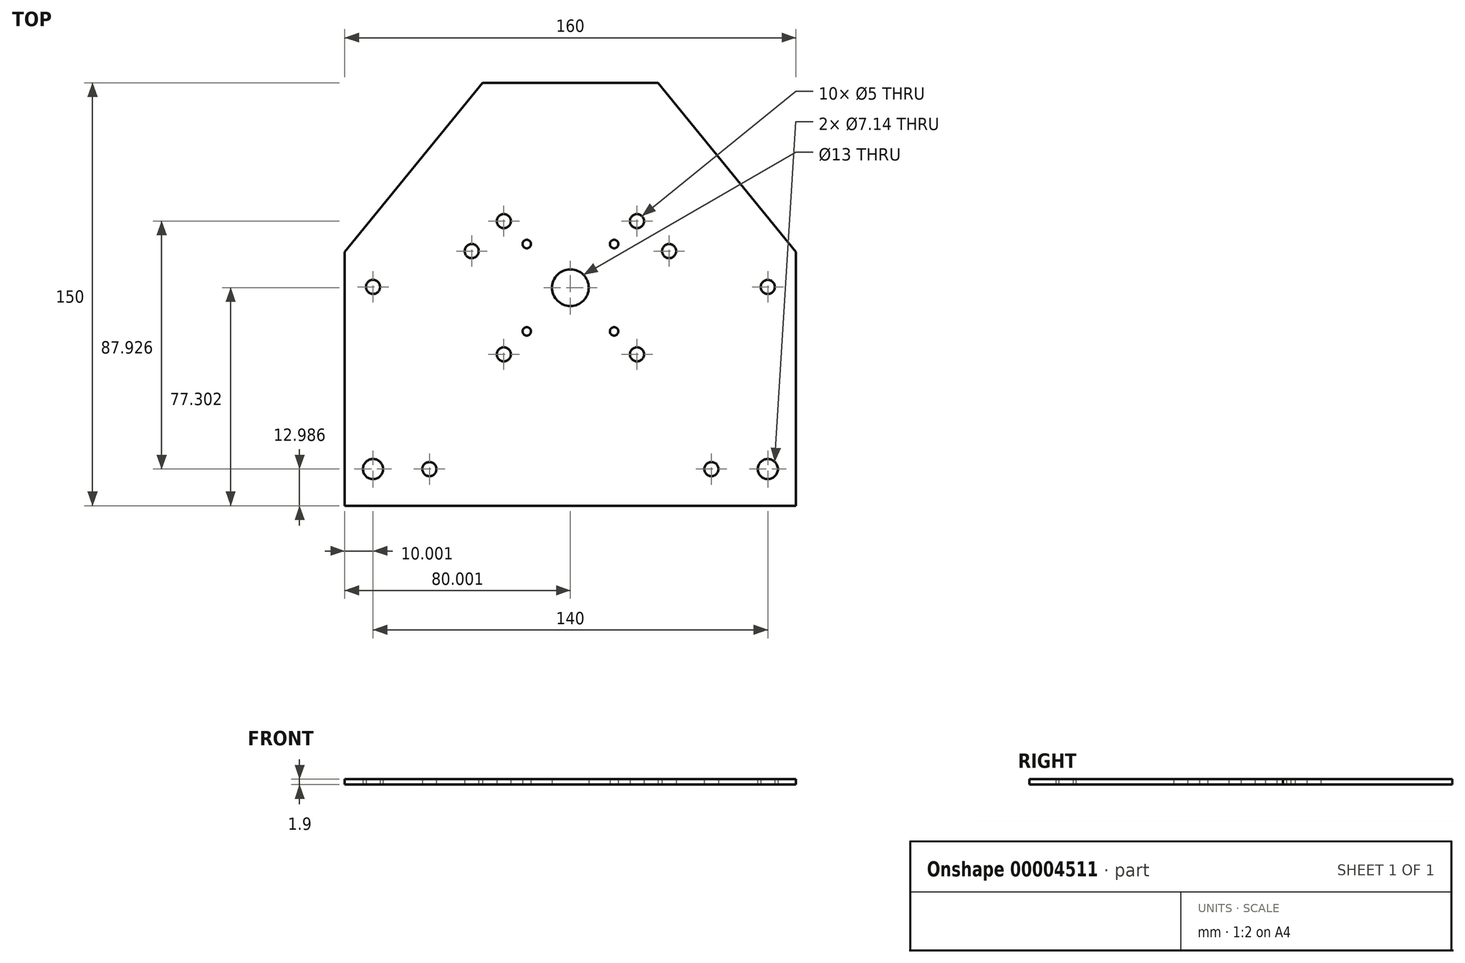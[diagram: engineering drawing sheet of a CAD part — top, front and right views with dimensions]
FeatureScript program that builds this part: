
annotation { "Feature Type Name" : "Feature", "Feature Type Description" : "" }
export const myFeature = defineFeature(function(context is Context, id is Id, definition is map)
    precondition{}
    {
        {
            var Q0;
            Q0=qCreatedBy(makeId("Top.planeOp"),FACE);
            var sketch = newSketch(context, id + "F0", { "sketchPlane" : qUnion([Q0])});
            skLineSegment(sketch, "E0.rect.left", {"start": v(-80.02, 15.3) * mm, "end": v(-80.02, -74.7) * mm});
            skLineSegment(sketch, "E0.rect.right", {"start": v(79.98, 15.3) * mm, "end": v(79.98, -74.7) * mm});
            skPoint(sketch, "E0.rect.middle", {"position": v(0, 0) * mm});
            skLineSegment(sketch, "E1", {"start": v(-80.02, 15.3) * mm, "end": v(-31.13, 75.3) * mm});
            skLineSegment(sketch, "E2", {"start": v(31.09, 75.3) * mm, "end": v(79.98, 15.3) * mm});
            skLineSegment(sketch, "E3", {"start": v(-0.02, 75.3) * mm, "end": v(-0.02, -74.7) * mm, "construction": true});
            skCircle(sketch, "E4", {"center": v(-70.02, -61.71) * mm, "radius": 3.57 * mm});
            skCircle(sketch, "E5", {"center": v(-50.02, -61.71) * mm, "radius": 2.5 * mm});
            skLineSegment(sketch, "E6", {"start": v(-70.02, -61.71) * mm, "end": v(-80.02, -61.71) * mm, "construction": true});
            skLineSegment(sketch, "E7", {"start": v(-70.02, -61.71) * mm, "end": v(-70.02, -74.41) * mm, "construction": true});
            skLineSegment(sketch, "E8", {"start": v(-50.02, -61.71) * mm, "end": v(-80.02, -61.71) * mm, "construction": true});
            skLineSegment(sketch, "E9", {"start": v(-50.02, -61.71) * mm, "end": v(-50.02, -74.41) * mm, "construction": true});
            skCircle(sketch, "E10", {"center": v(-70.02, 2.89) * mm, "radius": 2.5 * mm});
            skLineSegment(sketch, "E11", {"start": v(-70.02, 2.89) * mm, "end": v(-80.02, 2.89) * mm, "construction": true});
            skLineSegment(sketch, "E12", {"start": v(-70.02, 2.89) * mm, "end": v(-70.02, -74.41) * mm, "construction": true});
            skCircle(sketch, "E13", {"center": v(-35.02, 15.59) * mm, "radius": 2.5 * mm});
            skLineSegment(sketch, "E14", {"start": v(-35.02, 15.59) * mm, "end": v(-80.02, 15.59) * mm, "construction": true});
            skLineSegment(sketch, "E15", {"start": v(-35.02, 15.59) * mm, "end": v(-35.02, -74.41) * mm, "construction": true});
            skLineSegment(sketch, "E16", {"start": v(-31.13, 75.3) * mm, "end": v(-0.02, 75.3) * mm});
            skLineSegment(sketch, "E17", {"start": v(-0.02, 75.3) * mm, "end": v(31.09, 75.3) * mm});
            skCircle(sketch, "E18.0.MirrorC", {"center": v(69.98, -61.71) * mm, "radius": 3.57 * mm});
            skCircle(sketch, "E18.1.MirrorC", {"center": v(49.98, -61.71) * mm, "radius": 2.5 * mm});
            skCircle(sketch, "E18.2.MirrorC", {"center": v(34.98, 15.59) * mm, "radius": 2.5 * mm});
            skCircle(sketch, "E18.3.MirrorC", {"center": v(69.98, 2.89) * mm, "radius": 2.5 * mm});
            skLineSegment(sketch, "E19", {"start": v(-80.02, -74.7) * mm, "end": v(-0.02, -74.7) * mm});
            skLineSegment(sketch, "E20", {"start": v(-0.02, -74.7) * mm, "end": v(79.98, -74.7) * mm});
            skCircle(sketch, "E21", {"center": v(-23.63, -21.03) * mm, "radius": 2.5 * mm});
            skLineSegment(sketch, "E22", {"start": v(-23.63, -21.03) * mm, "end": v(-80.02, -21.03) * mm, "construction": true});
            skLineSegment(sketch, "E23", {"start": v(-23.63, -21.03) * mm, "end": v(-23.63, -74.7) * mm, "construction": true});
            skCircle(sketch, "E24.0.MirrorC", {"center": v(23.6, -21.03) * mm, "radius": 2.5 * mm});
            skCircle(sketch, "E25", {"center": v(-23.63, 26.21) * mm, "radius": 2.5 * mm});
            skLineSegment(sketch, "E26", {"start": v(-23.63, -74.7) * mm, "end": v(-23.63, 26.21) * mm, "construction": true});
            skCircle(sketch, "E27.0.MirrorC", {"center": v(23.6, 26.21) * mm, "radius": 2.5 * mm});
            skCircle(sketch, "E28", {"center": v(-15.5, -12.89) * mm, "radius": 1.5 * mm});
            skLineSegment(sketch, "E29", {"start": v(-15.5, -12.89) * mm, "end": v(-15.5, -74.7) * mm, "construction": true});
            skLineSegment(sketch, "E30", {"start": v(-15.5, -12.89) * mm, "end": v(-80.02, -12.89) * mm, "construction": true});
            skCircle(sketch, "E31.0.MirrorC", {"center": v(15.47, -12.89) * mm, "radius": 1.5 * mm});
            skCircle(sketch, "E32", {"center": v(-15.5, 18.1) * mm, "radius": 1.5 * mm});
            skLineSegment(sketch, "E33", {"start": v(-15.5, -74.7) * mm, "end": v(-15.5, 18.1) * mm, "construction": true});
            skCircle(sketch, "E34.0.MirrorC", {"center": v(15.47, 18.1) * mm, "radius": 1.5 * mm});
            skCircle(sketch, "E35", {"center": v(-0.02, 2.6) * mm, "radius": 6.5 * mm});
            skLineSegment(sketch, "E36", {"start": v(-0.02, 2.6) * mm, "end": v(-0.02, -74.7) * mm});
            skSolve(sketch);
        }
        {
            var Q0;
            Q0=makeQuery(id+"F0.imprint","IMPRINT",FACE,{"disambiguationData":[TD([[makeQuery(id+"F0.imprint","IMPRINT",EDGE,{"derivedFrom":sQuery(id+"F0.wireOp",EDGE,"E0.rect.left")}),1.0]])]});
            extrude(context, id + "F1", {"entities" : qUnion([Q0]), "depth" : 1.9 * mm});
        }
    });
